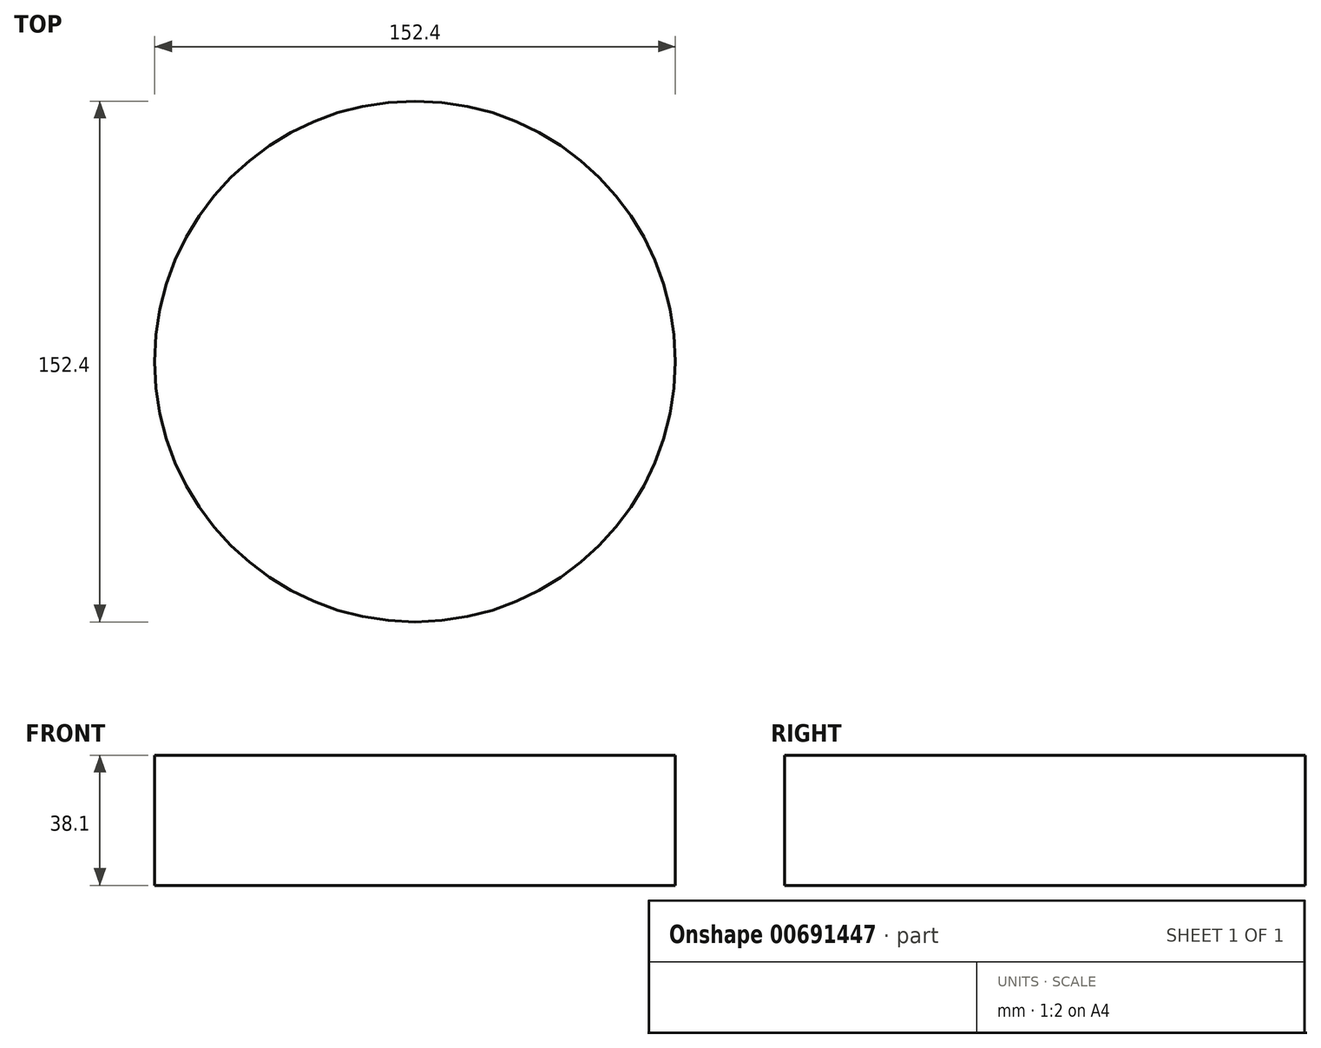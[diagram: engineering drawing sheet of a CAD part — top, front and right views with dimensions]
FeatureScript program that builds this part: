
annotation { "Feature Type Name" : "Feature", "Feature Type Description" : "" }
export const myFeature = defineFeature(function(context is Context, id is Id, definition is map)
    precondition{}
    {
        {
            var Q0;
            Q0=qCreatedBy(makeId("Top.planeOp"),FACE);
            var sketch = newSketch(context, id + "F0", { "sketchPlane" : qUnion([Q0])});
            skCircle(sketch, "E0", {"center": v(0, 0) * mm, "radius": 76.2 * mm});
            skSolve(sketch);
        }
        {
            var Q0;
            Q0=makeQuery(id+"F0.imprint","IMPRINT",FACE,{"disambiguationData":[TD([[makeQuery(id+"F0.imprint","IMPRINT",EDGE,{"derivedFrom":sQuery(id+"F0.wireOp",EDGE,"E0")}),1.0]])]});
            extrude(context, id + "F1", {"entities" : qUnion([Q0]), "depth" : 38.1 * mm, "offsetDistance" : 25.4 * mm});
        }
    });
